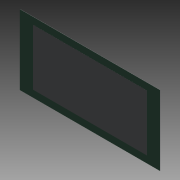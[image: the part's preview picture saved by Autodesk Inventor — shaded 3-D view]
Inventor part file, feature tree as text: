
AUTODESK INVENTOR PART (.ipt)
format: ipt  version: 2013 (Build 170138000, 138)  size: 82,432 bytes
history: native  units: in
note: dims shown in document units (in); Inventor stores cm internally (conversion verified against a paired STEP export)
features: extrude x2, sketch x2
ambient origin geometry x8: Origin, YZ Plane, XZ Plane, XY Plane, X Axis, Y Axis, Z Axis, Center Point
bodies: Solid1 (feature_tree)
feature tree (4):
  extrude  "Extrusion1"  Depth=400.0in
  extrude  "Extrusion2"  Depth=649.48in
  sketch  "Sketch1"  dims[d0=800.0in d1=400.0in]
  sketch  "Sketch2"  dims[d2=1.0in d3=0.0in d4=649.48in d6=321.47in d7=0.1in d8=0.0in]
